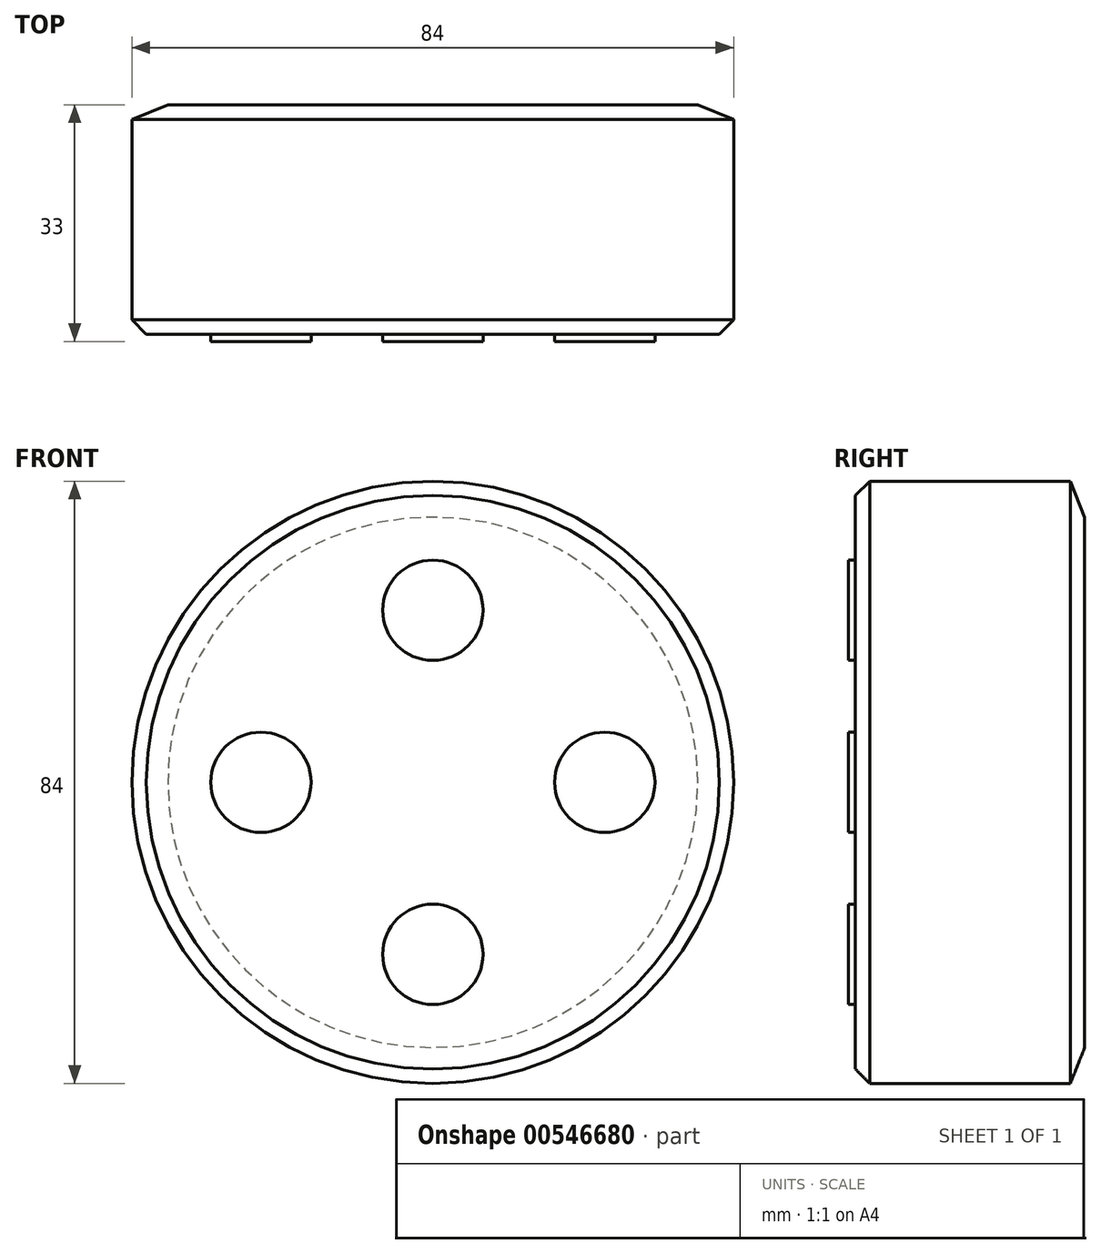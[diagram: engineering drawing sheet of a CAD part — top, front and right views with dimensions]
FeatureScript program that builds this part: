
annotation { "Feature Type Name" : "Feature", "Feature Type Description" : "" }
export const myFeature = defineFeature(function(context is Context, id is Id, definition is map)
    precondition{}
    {
        {
            var Q0;
            Q0=qCreatedBy(makeId("Front.planeOp"),FACE);
            var sketch = newSketch(context, id + "F0", { "sketchPlane" : qUnion([Q0])});
            skCircle(sketch, "E0", {"center": v(0, 0) * mm, "radius": 42 * mm});
            skSolve(sketch);
        }
        {
            var Q0;
            Q0 = qSketchRegion(id + "F0", true);
            extrude(context, id + "F1", {"entities" : qUnion([Q0]), "depth" : 32 * mm, "offsetDistance" : 25 * mm});
        }
        {
            var Q0;
            Q0=makeQuery(id+"F1.opExtrude","CAP_FACE",FACE,{"disambiguationData":[OSD([sQuery(id+"F0.wireOp",EDGE,"E0")])],"isStart":true});
            chamfer(context, id + "F2", {"entities" : qUnion([Q0]), "chamferType" : ChamferType.TWO_OFFSETS, "width1" : 2 * mm, "oppositeDirection" : false, "width2" : 5 * mm, "tangentPropagation" : true});
        }
        {
            var Q0;
            Q0=makeQuery(id+"F1.opExtrude","CAP_FACE",FACE,{"disambiguationData":[OSD([sQuery(id+"F0.wireOp",EDGE,"E0")])],"isStart":false});
            chamfer(context, id + "F3", {"entities" : qUnion([Q0]), "width" : 2 * mm, "tangentPropagation" : true});
        }
        {
            var Q0;
            Q0=makeQuery(id+"F1.opExtrude","CAP_FACE",FACE,{"disambiguationData":[OSD([sQuery(id+"F0.wireOp",EDGE,"E0")])],"isStart":false});
            var sketch = newSketch(context, id + "F4", { "sketchPlane" : qUnion([Q0])});
            skLineSegment(sketch, "E1", {"start": v(-69.27, 0) * mm, "end": v(62.97, 0) * mm, "construction": true});
            skLineSegment(sketch, "E2", {"start": v(0, 50.92) * mm, "end": v(0, -47.46) * mm, "construction": true});
            skCircle(sketch, "E3", {"center": v(-24, 0) * mm, "radius": 7 * mm});
            skCircle(sketch, "E4.MirrorC", {"center": v(24, 0) * mm, "radius": 7 * mm});
            skCircle(sketch, "E5", {"center": v(0, 0) * mm, "radius": 24 * mm, "construction": true});
            skCircle(sketch, "E6", {"center": v(0, 24) * mm, "radius": 7 * mm});
            skCircle(sketch, "E7.MirrorC", {"center": v(0, -24) * mm, "radius": 7 * mm});
            skSolve(sketch);
        }
        {
            var Q0;
            Q0 = qSketchRegion(id + "F4", true);
            extrude(context, id + "F5", {"entities" : qUnion([Q0]), "operationType" : NewBodyOperationType.ADD, "depth" : 1 * mm, "offsetDistance" : 25 * mm});
        }
    });
